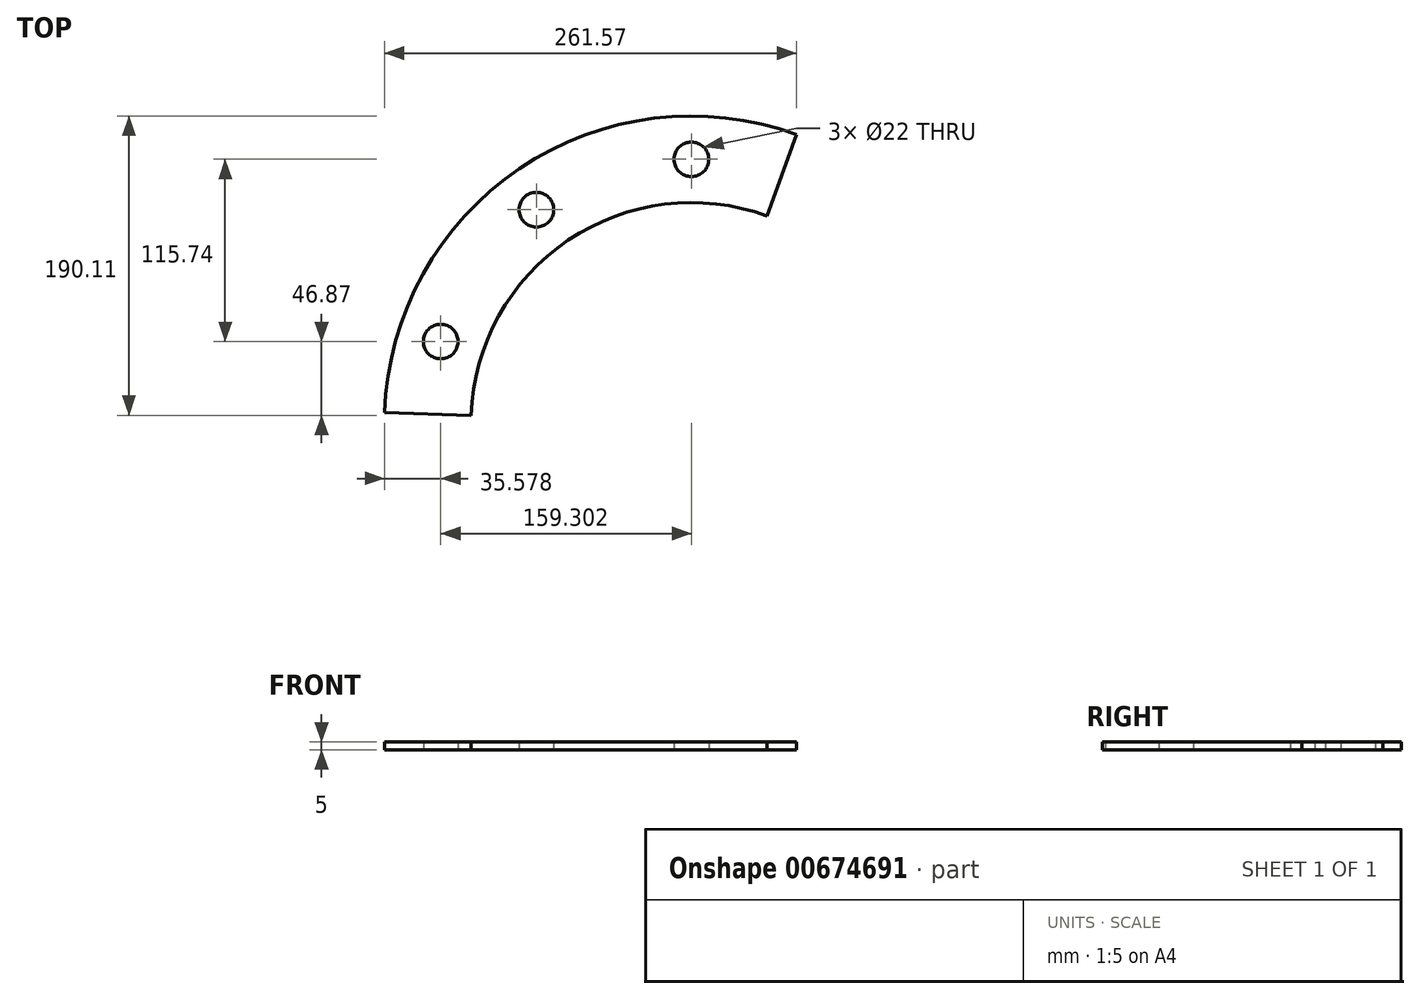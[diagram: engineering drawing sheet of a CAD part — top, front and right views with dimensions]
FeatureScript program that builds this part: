
annotation { "Feature Type Name" : "Feature", "Feature Type Description" : "" }
export const myFeature = defineFeature(function(context is Context, id is Id, definition is map)
    precondition{}
    {
        {
            var Q0;
            Q0=qCreatedBy(makeId("Top.planeOp"),FACE);
            var sketch = newSketch(context, id + "F0", { "sketchPlane" : qUnion([Q0])});
            skCircle(sketch, "E0", {"center": v(0, 0) * mm, "radius": 195 * mm});
            skLineSegment(sketch, "E1", {"start": v(-236.95, 0) * mm, "end": v(264.25, 0) * mm, "construction": true});
            skLineSegment(sketch, "E2", {"start": v(0, -228.62) * mm, "end": v(0, 236.65) * mm, "construction": true});
            skCircle(sketch, "E3", {"center": v(0, 0) * mm, "radius": 140 * mm});
            skCircle(sketch, "E4", {"center": v(0, 0) * mm, "radius": 167.5 * mm});
            skPoint(sketch, "E5", {"position": v(0, 167.5) * mm});
            skPoint(sketch, "E6.1.0", {"position": v(-98.45, 135.51) * mm});
            skPoint(sketch, "E6.2.0", {"position": v(-159.3, 51.76) * mm});
            skPoint(sketch, "E6.3.0", {"position": v(-159.3, -51.76) * mm});
            skPoint(sketch, "E6.4.0", {"position": v(-98.45, -135.51) * mm});
            skPoint(sketch, "E6.5.0", {"position": v(0, -167.5) * mm});
            skPoint(sketch, "E6.6.0", {"position": v(98.45, -135.51) * mm});
            skPoint(sketch, "E6.7.0", {"position": v(159.3, -51.76) * mm});
            skPoint(sketch, "E6.8.0", {"position": v(159.3, 51.76) * mm});
            skPoint(sketch, "E6.9.0", {"position": v(98.45, 135.51) * mm});
            skLineSegment(sketch, "E7", {"start": v(0, 0) * mm, "end": v(91.1, 250.3) * mm});
            skLineSegment(sketch, "E8", {"start": v(0, 0) * mm, "end": v(-87.39, -240.1) * mm});
            skLineSegment(sketch, "E9", {"start": v(0, 0) * mm, "end": v(-255.48, 8.92) * mm});
            skLineSegment(sketch, "E10", {"start": v(0, 0) * mm, "end": v(300.02, -10.48) * mm});
            skSolve(sketch);
        }
        {
            var Q0;
            {var subQ0=sQuery(id+"F0.wireOp",EDGE,"E9");var subQ1=sQuery(id+"F0.wireOp",EDGE,"E3");var subQ2=makeQuery(id+"F0.imprint","INTERSECT",VERTEX,{"derivedFrom":[subQ1,subQ0]});Q0=makeQuery(id+"F0.imprint","IMPRINT",FACE,{"disambiguationData":[TD([[makeQuery(id+"F0.imprint","IMPRINT",EDGE,{"disambiguationData":[TD([[subQ2,1.0]])],"derivedFrom":subQ1}),-1.0]])]});}
            var Q1;
            {var subQ0=sQuery(id+"F0.wireOp",EDGE,"E9");var subQ1=sQuery(id+"F0.wireOp",EDGE,"E0");var subQ2=makeQuery(id+"F0.imprint","INTERSECT",VERTEX,{"derivedFrom":[subQ1,subQ0]});Q1=makeQuery(id+"F0.imprint","IMPRINT",FACE,{"disambiguationData":[TD([[makeQuery(id+"F0.imprint","IMPRINT",EDGE,{"disambiguationData":[TD([[subQ2,1.0]])],"derivedFrom":subQ1}),1.0]])]});}
            extrude(context, id + "F1", {"entities" : qUnion([Q0, Q1]), "depth" : 5 * mm, "offsetDistance" : 25 * mm});
        }
        {
            var Q0;
            Q0=sQuery(id+"F0.wireOp",VERTEX,"E5");
            var Q1;
            Q1=sQuery(id+"F0.wireOp",VERTEX,"E6.1.0");
            var Q2;
            Q2=sQuery(id+"F0.wireOp",VERTEX,"E6.2.0");
            var Q3;
            Q3=makeQuery(id+"F1.opExtrude","SWEPT_BODY",BODY,{"disambiguationData":[OSD([sQuery(id+"F0.wireOp",EDGE,"E0"),sQuery(id+"F0.wireOp",EDGE,"E3"),sQuery(id+"F0.wireOp",EDGE,"E7"),sQuery(id+"F0.wireOp",EDGE,"7779584a-14d0-4c0c-a12f-be6d3e54e7f4.3.0")])]});
            hole(context, id + "F2", {"style" : HoleStyle.SIMPLE, "endStyle" : HoleEndStyle.THROUGH, "oppositeDirection" : true, "standardTappedOrClearance" : lookupTablePath({ "standard" : "ISO", "size" : "22", "type" : "Drilled" }), "standardBlindInLast" : lookupTablePath({ "standard" : "ISO", "size" : "22", "type" : "Drilled" }), "holeDiameter" : 22 * mm, "majorDiameter" : 5 * mm, "tappedDepth" : 30 * mm, "tapClearance" : 3, "locations" : qUnion([Q0, Q1, Q2]), "scope" : qUnion([Q3])});
        }
    });
